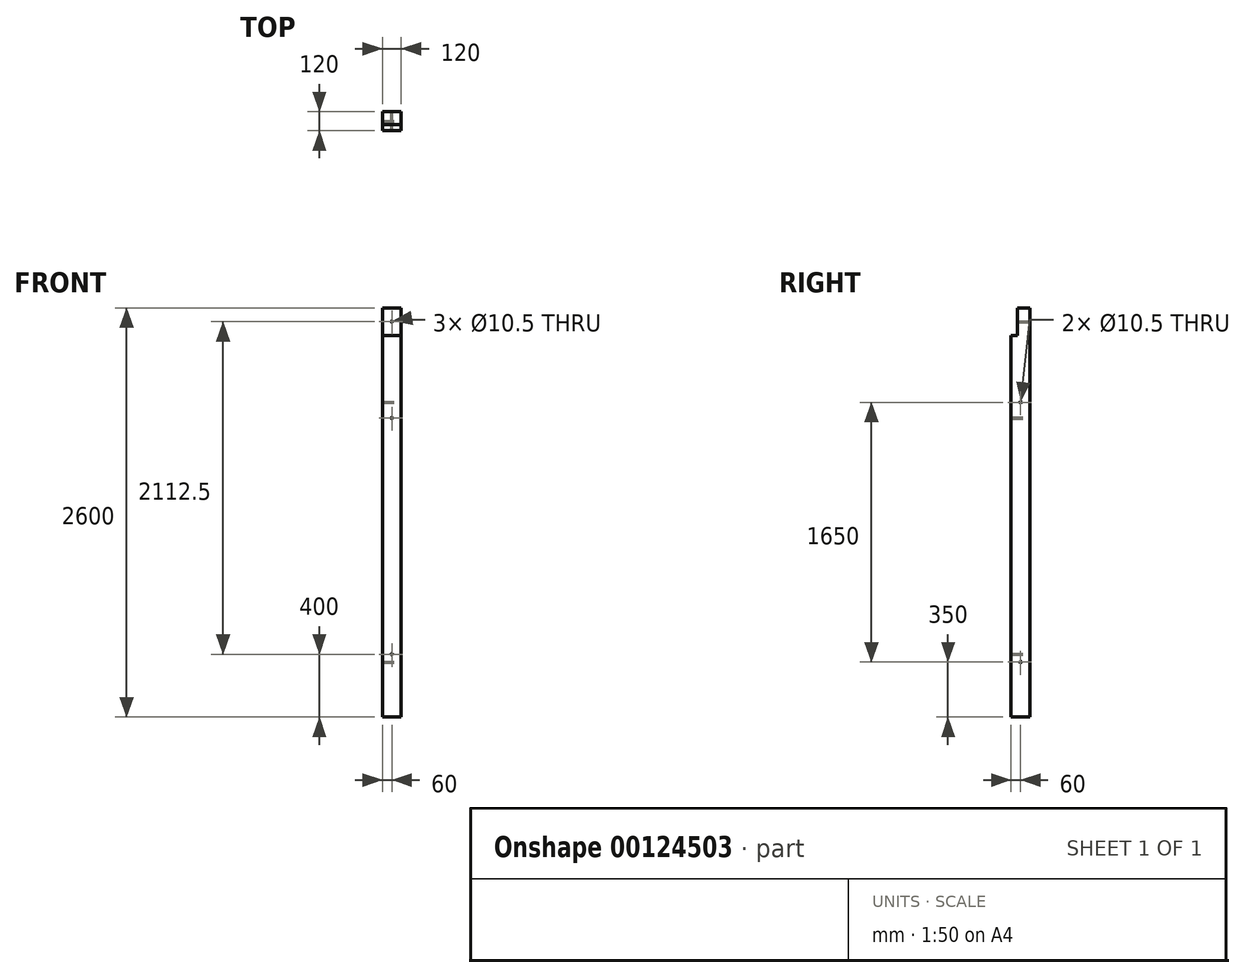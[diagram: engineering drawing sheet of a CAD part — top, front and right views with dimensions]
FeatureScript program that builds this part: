
annotation { "Feature Type Name" : "Feature", "Feature Type Description" : "" }
export const myFeature = defineFeature(function(context is Context, id is Id, definition is map)
    precondition{}
    {
        {
            var Q0;
            Q0=qCreatedBy(makeId("Top.planeOp"),FACE);
            var sketch = newSketch(context, id + "F0", { "sketchPlane" : qUnion([Q0])});
            skLineSegment(sketch, "E0", {"start": v(0, 0) * mm, "end": v(0, 330.83) * mm, "construction": true});
            skLineSegment(sketch, "E1", {"start": v(-296.67, 0) * mm, "end": v(360, 0) * mm, "construction": true});
            skLineSegment(sketch, "E2.bottom", {"start": v(60, 60) * mm, "end": v(-60, 60) * mm});
            skLineSegment(sketch, "E2.top", {"start": v(60, -60) * mm, "end": v(-60, -60) * mm});
            skLineSegment(sketch, "E2.left", {"start": v(60, 60) * mm, "end": v(60, -60) * mm});
            skLineSegment(sketch, "E2.right", {"start": v(-60, 60) * mm, "end": v(-60, -60) * mm});
            skPoint(sketch, "E2.middle", {"position": v(0, 0) * mm});
            skPoint(sketch, "E3.visualSharp", {"position": v(-60, 60) * mm});
            skPoint(sketch, "E4.visualSharp", {"position": v(60, 60) * mm});
            skPoint(sketch, "E5.visualSharp", {"position": v(-60, -60) * mm});
            skPoint(sketch, "E6.visualSharp", {"position": v(60, -60) * mm});
            skSolve(sketch);
        }
        {
            var Q0;
            Q0=qSketchRegion(id+"F0",true);
            extrude(context, id + "F1", {"entities" : qUnion([Q0]), "endBound" : BoundingType.SYMMETRIC, "depth" : 2600 * mm});
        }
        {
            var Q0;
            Q0=makeQuery(id+"F1.opExtrude","SWEPT_FACE",FACE,{"disambiguationData":[OSD([sQuery(id+"F0.wireOp",EDGE,"E2.left")])]});
            var sketch = newSketch(context, id + "F2", { "sketchPlane" : qUnion([Q0])});
            skLineSegment(sketch, "E7.bottom", {"start": v(-60, 1300) * mm, "end": v(-20, 1300) * mm});
            skLineSegment(sketch, "E7.top", {"start": v(-60, 1125) * mm, "end": v(-20, 1125) * mm});
            skLineSegment(sketch, "E7.left", {"start": v(-60, 1300) * mm, "end": v(-60, 1125) * mm});
            skLineSegment(sketch, "E7.right", {"start": v(-20, 1300) * mm, "end": v(-20, 1125) * mm});
            skSolve(sketch);
        }
        {
            var Q0;
            Q0=qSketchRegion(id+"F2",true);
            extrude(context, id + "F3", {"entities" : qUnion([Q0]), "operationType" : NewBodyOperationType.REMOVE, "endBound" : BoundingType.UP_TO_NEXT, "oppositeDirection" : true, "depth" : 25 * mm});
        }
        {
            var Q0;
            Q0=makeQuery(id+"F1.opExtrude","SWEPT_FACE",FACE,{"disambiguationData":[OSD([sQuery(id+"F0.wireOp",EDGE,"E2.bottom")])]});
            var sketch = newSketch(context, id + "F4", { "sketchPlane" : qUnion([Q0])});
            skCircle(sketch, "E8", {"center": v(0, 1212.5) * mm, "radius": 5.25 * mm});
            skCircle(sketch, "E9", {"center": v(0, -900) * mm, "radius": 5.25 * mm});
            skCircle(sketch, "E10", {"center": v(0, 600) * mm, "radius": 5.25 * mm});
            skSolve(sketch);
        }
        {
            var Q0;
            Q0 = qSketchRegion(id + "F4", true);
            extrude(context, id + "F5", {"entities" : qUnion([Q0]), "operationType" : NewBodyOperationType.REMOVE, "endBound" : BoundingType.THROUGH_ALL, "oppositeDirection" : true, "depth" : 25 * mm});
        }
        {
            var Q0;
            Q0=makeQuery(id+"F1.opExtrude","SWEPT_FACE",FACE,{"disambiguationData":[OSD([sQuery(id+"F0.wireOp",EDGE,"E2.left")])]});
            var sketch = newSketch(context, id + "F6", { "sketchPlane" : qUnion([Q0])});
            skCircle(sketch, "E11", {"center": v(0, -950) * mm, "radius": 5.25 * mm});
            skCircle(sketch, "E12", {"center": v(0, 700) * mm, "radius": 5.25 * mm});
            skSolve(sketch);
        }
        {
            var Q0;
            Q0 = qSketchRegion(id + "F6", true);
            extrude(context, id + "F7", {"entities" : qUnion([Q0]), "operationType" : NewBodyOperationType.REMOVE, "endBound" : BoundingType.THROUGH_ALL, "oppositeDirection" : true, "depth" : 25 * mm});
        }
    });
